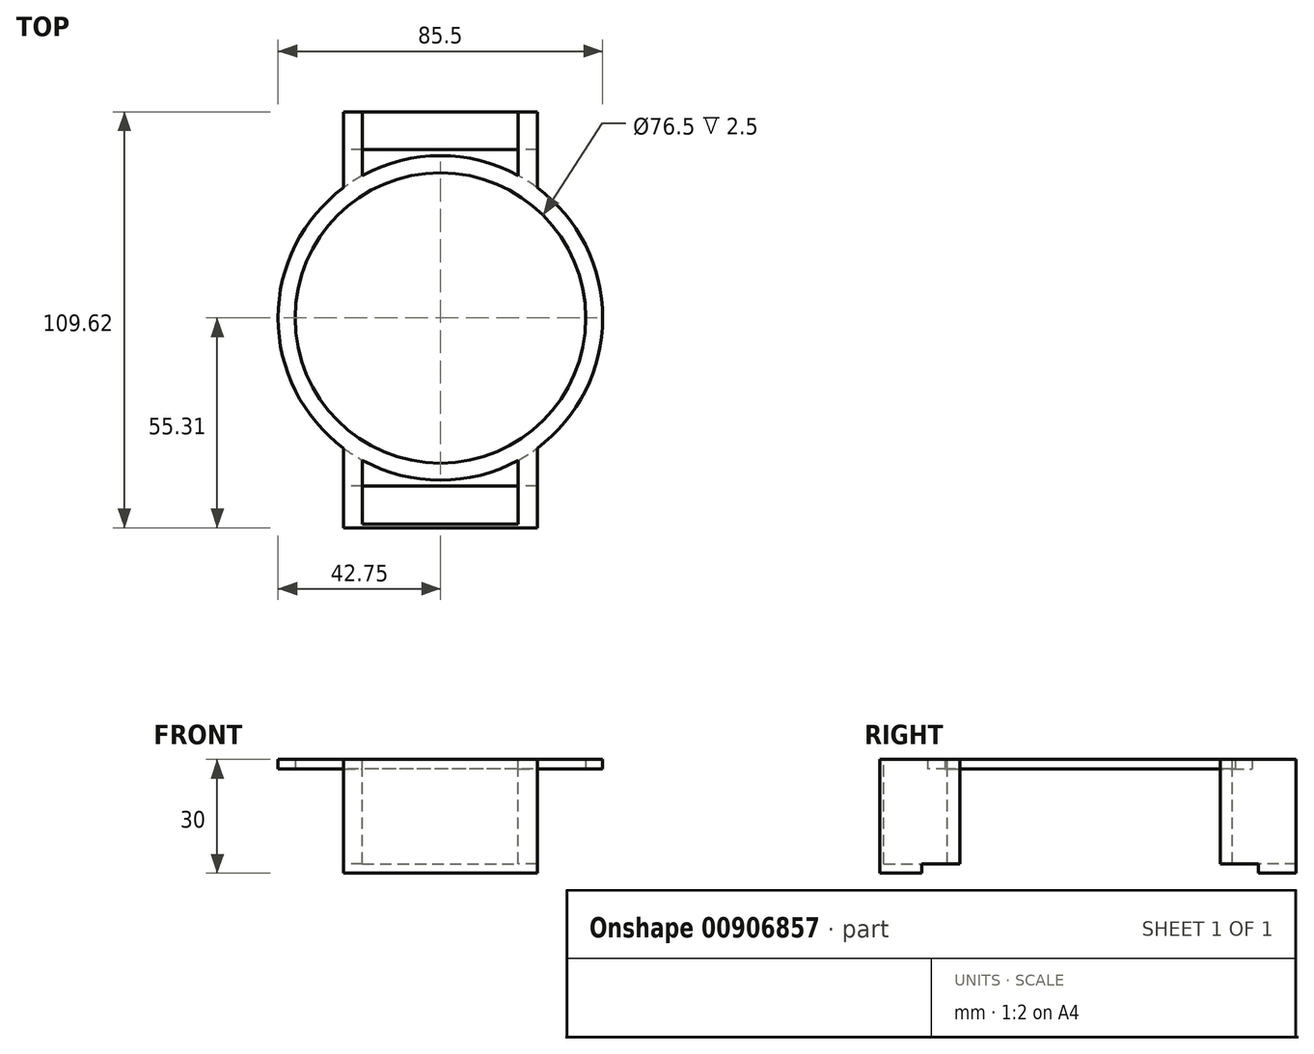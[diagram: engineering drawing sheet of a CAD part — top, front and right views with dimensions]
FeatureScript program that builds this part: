
annotation { "Feature Type Name" : "Feature", "Feature Type Description" : "" }
export const myFeature = defineFeature(function(context is Context, id is Id, definition is map)
    precondition{}
    {
        {
            var Q0;
            Q0=qCreatedBy(makeId("Top.planeOp"),FACE);
            var sketch = newSketch(context, id + "F0", { "sketchPlane" : qUnion([Q0])});
            skCircle(sketch, "E0", {"center": v(0, 0) * mm, "radius": 38.25 * mm});
            skCircle(sketch, "E1", {"center": v(0, 0) * mm, "radius": 42.75 * mm});
            skSolve(sketch);
        }
        {
            var Q0;
            Q0 = qSketchRegion(id + "F0", true);
            extrude(context, id + "F1", {"entities" : qUnion([Q0]), "depth" : 2.5 * mm, "offsetDistance" : 25 * mm});
        }
        {
            var Q0;
            Q0=makeQuery(id+"F1.opExtrude","CAP_FACE",FACE,{"disambiguationData":[OSD([sQuery(id+"F0.wireOp",EDGE,"E0"),sQuery(id+"F0.wireOp",EDGE,"E1")])],"isStart":false});
            var sketch = newSketch(context, id + "F2", { "sketchPlane" : qUnion([Q0])});
            skLineSegment(sketch, "E2", {"start": v(0, 0) * mm, "end": v(43.53, 43.53) * mm, "construction": true});
            skLineSegment(sketch, "E3.MirrorCS", {"start": v(0, 0) * mm, "end": v(43.53, -43.53) * mm, "construction": true});
            skLineSegment(sketch, "E4", {"start": v(25.5, -34.31) * mm, "end": v(25.5, -54.31) * mm});
            skLineSegment(sketch, "E5", {"start": v(25.5, -54.31) * mm, "end": v(20.5, -54.31) * mm});
            skLineSegment(sketch, "E6", {"start": v(20.5, -54.31) * mm, "end": v(20.5, -37.51) * mm});
            skArc(sketch, "E7", {"start": v(25.5, -34.31) * mm, "mid": v(23.06, -36) * mm, "end": v(20.5, -37.51) * mm});
            skLineSegment(sketch, "E8.MirrorCS", {"start": v(-25.5, -34.31) * mm, "end": v(-25.5, -54.31) * mm});
            skLineSegment(sketch, "E9.MirrorCS", {"start": v(-25.5, -54.31) * mm, "end": v(-20.5, -54.31) * mm});
            skLineSegment(sketch, "E10.MirrorCS", {"start": v(-20.5, -54.31) * mm, "end": v(-20.5, -37.51) * mm});
            skArc(sketch, "E11.MirrorCS", {"start": v(-25.5, -34.31) * mm, "mid": v(-23.06, -36) * mm, "end": v(-20.5, -37.51) * mm});
            skArc(sketch, "E12.MirrorCS", {"start": v(25.5, 34.31) * mm, "mid": v(23.06, 36) * mm, "end": v(20.5, 37.51) * mm});
            skLineSegment(sketch, "E13.MirrorCS", {"start": v(20.5, 54.31) * mm, "end": v(20.5, 37.51) * mm});
            skLineSegment(sketch, "E14.MirrorCS", {"start": v(25.5, 54.31) * mm, "end": v(20.5, 54.31) * mm});
            skLineSegment(sketch, "E15.MirrorCS", {"start": v(25.5, 34.31) * mm, "end": v(25.5, 54.31) * mm});
            skLineSegment(sketch, "E16.MirrorCS", {"start": v(-25.5, 54.31) * mm, "end": v(-20.5, 54.31) * mm});
            skArc(sketch, "E17.MirrorCS", {"start": v(-25.5, 34.31) * mm, "mid": v(-23.06, 36) * mm, "end": v(-20.5, 37.51) * mm});
            skLineSegment(sketch, "E18.MirrorCS", {"start": v(-25.5, 34.31) * mm, "end": v(-25.5, 54.31) * mm});
            skLineSegment(sketch, "E19.MirrorCS", {"start": v(-20.5, 54.31) * mm, "end": v(-20.5, 37.51) * mm});
            skSolve(sketch);
        }
        {
            var Q0;
            Q0 = qSketchRegion(id + "F2", true);
            extrude(context, id + "F3", {"entities" : qUnion([Q0]), "operationType" : NewBodyOperationType.ADD, "oppositeDirection" : true, "depth" : 27.5 * mm, "offsetDistance" : 25 * mm});
        }
        {
            var Q0;
            Q0=makeQuery(id+"F3.opExtrude","CAP_FACE",FACE,{"disambiguationData":[OSD([sQuery(id+"F2.wireOp",EDGE,"E18.MirrorCS"),sQuery(id+"F2.wireOp",EDGE,"E16.MirrorCS"),sQuery(id+"F2.wireOp",EDGE,"E19.MirrorCS"),sQuery(id+"F2.wireOp",EDGE,"E17.MirrorCS")])],"isStart":false});
            var sketch = newSketch(context, id + "F4", { "sketchPlane" : qUnion([Q0])});
            skLineSegment(sketch, "E20", {"start": v(-25.5, -54.31) * mm, "end": v(25.5, -54.31) * mm});
            skLineSegment(sketch, "E21", {"start": v(25.5, -54.31) * mm, "end": v(25.5, -44.31) * mm});
            skLineSegment(sketch, "E22", {"start": v(25.5, -44.31) * mm, "end": v(-25.5, -44.31) * mm});
            skLineSegment(sketch, "E23", {"start": v(-25.5, -44.31) * mm, "end": v(-25.5, -54.31) * mm});
            skLineSegment(sketch, "E24.MirrorCS", {"start": v(-25.5, 44.31) * mm, "end": v(-25.5, 54.31) * mm});
            skLineSegment(sketch, "E25.MirrorCS", {"start": v(25.5, 44.31) * mm, "end": v(-25.5, 44.31) * mm});
            skLineSegment(sketch, "E26.MirrorCS", {"start": v(25.5, 54.31) * mm, "end": v(25.5, 44.31) * mm});
            skLineSegment(sketch, "E27.MirrorCS", {"start": v(-25.5, 54.31) * mm, "end": v(25.5, 54.31) * mm});
            skSolve(sketch);
        }
        {
            var Q0;
            Q0 = qSketchRegion(id + "F4", true);
            extrude(context, id + "F5", {"entities" : qUnion([Q0]), "operationType" : NewBodyOperationType.ADD, "depth" : 2.5 * mm, "offsetDistance" : 25 * mm});
        }
        {
            var Q0;
            Q0=makeQuery(id+"F5.boolean.opBoolean","MERGE",FACE,{"derivedFrom":[makeQuery(id+"F3.opExtrude","SWEPT_FACE",FACE,{"disambiguationData":[OSD([sQuery(id+"F2.wireOp",EDGE,"E9.MirrorCS")])]}),makeQuery(id+"F3.opExtrude","SWEPT_FACE",FACE,{"disambiguationData":[OSD([sQuery(id+"F2.wireOp",EDGE,"E5")])]}),makeQuery(id+"F5.opExtrude","SWEPT_FACE",FACE,{"disambiguationData":[OSD([sQuery(id+"F4.wireOp",EDGE,"E27.MirrorCS")])]})]});
            var sketch = newSketch(context, id + "F6", { "sketchPlane" : qUnion([Q0])});
            skLineSegment(sketch, "E28.bottom", {"start": v(-25.5, 2.5) * mm, "end": v(25.5, 2.5) * mm});
            skLineSegment(sketch, "E28.top", {"start": v(-25.5, -27.5) * mm, "end": v(25.5, -27.5) * mm});
            skLineSegment(sketch, "E28.left", {"start": v(-25.5, 2.5) * mm, "end": v(-25.5, -27.5) * mm});
            skLineSegment(sketch, "E28.right", {"start": v(25.5, 2.5) * mm, "end": v(25.5, -27.5) * mm});
            skSolve(sketch);
        }
        {
            var Q0;
            Q0 = qSketchRegion(id + "F6", true);
            extrude(context, id + "F7", {"entities" : qUnion([Q0]), "operationType" : NewBodyOperationType.ADD, "depth" : 1 * mm, "offsetDistance" : 25 * mm});
        }
    });
